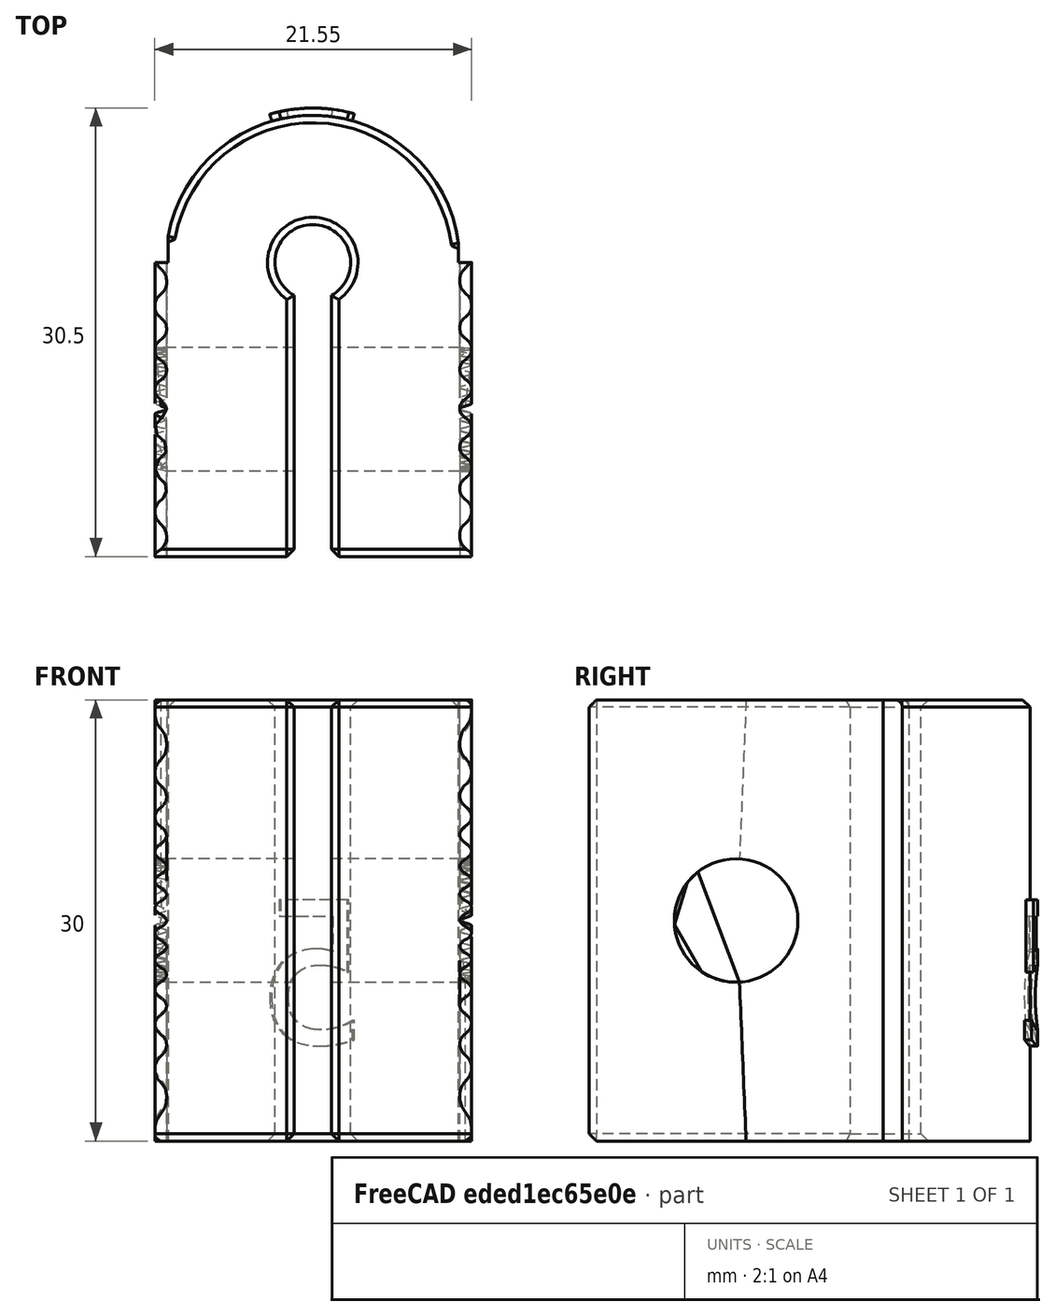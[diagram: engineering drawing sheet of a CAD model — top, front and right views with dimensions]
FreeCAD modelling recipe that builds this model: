
FCSTD DOCUMENT  (FreeCAD 1.1R42945 (Git))
Label: Pin clamp
License: All rights reserved
LicenseURL: https://en.wikipedia.org/wiki/All_rights_reserved
objects: Part::FeaturePython×3, App::Point×3, PartDesign::Body×3, Sketcher::SketchObject×2, PartDesign::FeatureBase×2, Mesh::Feature×1, Spreadsheet::Sheet×1, Part::RuledSurface×1, Part::Extrusion×1, Part::Box×1, Part::MultiCommon×1, Part::Part2DObjectPython×1, Part::Cylinder×1, PartDesign::Pad×1, Part::MultiFuse×1, Part::Chamfer×1, Part::Cut×1
note: 26 computed .brp shape members not serialized (recipe doc carries the construction recipe); baked Part::Feature solids carry a one-line shape summary decoded from their .brp

FEATURE [Mesh::Feature] PINCLAMP_5MM
  Placement = pos=(0,0,-30) rot=(0,0,-1;1.5708rad)
FEATURE [Spreadsheet::Sheet] Spreadsheet  label="Parameters"
  cells = A1='Description of parameter; B1='Measurement; A2='Bolt diameter (mm); B2(bolt)=8; A3='Bolt diameter tolerance (mm); B3(BoltTolerance)=0.4; A4='Pin diameter (mm); B4(pin)=5; A5='Pin diameter tolerance (mm); B5(PinTolerance)=0.15; A7='Interface parameters; A8='Inner radius; B8(InnerRadius)=2; A9='Outer radius; B9(OuterRadius)=20; A10='Amplitude of waves; B10(amplitude)=0.8; A11='Number of waves; B11(NumberOfWaves)=36; A12='Interval (do not change); B12(Interval)=0.01
FEATURE [Part::FeaturePython] ParametricCurve  # WARN: FeaturePython — macro-defined, semantics opaque (R4)
  AttacherType = Attacher::AttachEngine3D
  Closed = false
  Continuity = C2
  EditFormulas = false
  F_X = 0
  F_Y = 0
  F_Z = 0
  F_a = 20
  F_b = 36
  F_c = 0.8
  F_d = [0,0]
  FormulaName = formula1
  Formulas = 0
  Interval = 0.01
  MakeFace = false
  PlusOneIteration = true
  Points = (630) [(20,0,0.4),(19.999,0.199997,0.602621),(19.996,0.399973,0.738292),(19.991,0.59991,0.791969),(19.984,0.799787,0.799956),(19.975,0.999583,0.799593),+624 more]
  ShapeType = 0
  Sorted = false
  UpdateSpreadsheet = false
  UseSpreadsheet = false
  Version = 2023.05.06
  X = a*cos(t)
  Y = a*sin(t)
  Z = c * ( 3*((1 + sin(b*t))/2)^2 - 2*((1 + sin(b*t))/2)^3 )
  a = 20
  b = 36
  c = 0.8
  t_max = 6.28319
  t_min = 0
  expr: Interval = .Spreadsheet.Interval
FEATURE [Part::FeaturePython] ParametricCurve001  # WARN: FeaturePython — macro-defined, semantics opaque (R4)
  AttacherType = Attacher::AttachEngine3D
  Closed = false
  Continuity = C2
  EditFormulas = false
  F_X = 0
  F_Y = 0
  F_Z = 0
  F_a = 2
  F_b = 36
  F_c = 0.8
  F_d = [0,0]
  FormulaName = formula2
  Formulas = 0
  Interval = 0.01
  MakeFace = false
  PlusOneIteration = true
  Points = (630) [(2,0,0.4),(1.9999,0.0199997,0.602621),(1.9996,0.0399973,0.738292),(1.9991,0.059991,0.791969),(1.9984,0.0799787,0.799956),(1.9975,0.0999583,0.799593),+624 more]
  ShapeType = 0
  Sorted = false
  UpdateSpreadsheet = false
  UseSpreadsheet = false
  Version = 2023.05.06
  X = a*cos(t)
  Y = a*sin(t)
  Z = c * ( 3*((1 + sin(b*t))/2)^2 - 2*((1 + sin(b*t))/2)^3 )
  a = 2
  b = 36
  c = 0.8
  t_max = 6.28319
  t_min = 0
  expr: Interval = .Spreadsheet.Interval
  expr: a = .Spreadsheet.InnerRadius
  expr: b = .Spreadsheet.NumberOfWaves
  expr: c = .Spreadsheet.amplitude
FEATURE [Part::RuledSurface] Ruled_Surface
  Curve1 = -> ParametricCurve [Edge1]
  Curve2 = -> ParametricCurve001 [Edge1]
  Orientation = 0
  Placement = pos=(10,-4.94766,-14.9986) rot=(0.020938,0.999562,0.020938;1.57123rad)
FEATURE [Part::Extrusion] Extrude003
  Base = -> Ruled_Surface
  Dir = (-1,0,0)
  DirMode = 0
  FaceMakerClass = Part::FaceMakerBullseye
  FaceMakerMode = 3
  LengthFwd = 2
  LengthRev = 0
  Solid = false
  Symmetric = false
FEATURE [Part::Box] Box  label="Cube"
  AttacherType = Attacher::AttachEngine3D
  Height = 1.5
  Length = 30
  Placement = pos=(9.4513,-15,0) rot=(0,1,0;1.5708rad)
  Width = 20
FEATURE [Part::MultiCommon] Common
  Placement = pos=(0,0,-30) rot=(0,1,0;3.14159rad)
  Shapes = -> [Box,Extrude003]
FEATURE [Part::Part2DObjectPython] ShapeString  # Draft 2D object (typed FeaturePython)
  FontFile = <path>
  Fuse = false
  Justification = 4
  JustificationReference = 0
  KeepLeftMargin = false
  MakeFace = true
  ObliqueAngle = 0
  Placement = pos=(30,4.85425,0) rot=(0,0,1;0rad)
  ScaleToSize = true
  Size = 16
  String = 5
  Tracking = 0
FEATURE [Part::Cylinder] Cylinder
  Angle = 360
  AttacherType = Attacher::AttachEngine3D
  FirstAngle = 0
  Height = 30
  Placement = pos=(-15,-5,-15) rot=(0,1,0;1.5708rad)
  Radius = 4.2
  SecondAngle = 0
  expr: Radius = (Spreadsheet.bolt + Spreadsheet.BoltTolerance) / 2
FEATURE [Sketcher::SketchObject] Sketch
  ArcFitTolerance = 1e-06
  AttachmentSupport = -> [Origin]
  ExternalTypes = [0]
  FullyConstrained = false
  MakeInternals = false
  MapMode = 5
  expr: Constraints[16] = (Spreadsheet.pin + Spreadsheet.PinTolerance) / 2
  sketch-geometry (8):
    g0: LineSegment StartX=-9.84423 StartY=-15 StartZ=0 EndX=-9.84423 EndY=6.75819 EndZ=0
    g1: LineSegment StartX=-9.84423 StartY=-15 StartZ=0 EndX=-1.26513 EndY=-15 EndZ=0
    g2: LineSegment StartX=-1.26513 StartY=-15 StartZ=0 EndX=-1.26513 EndY=2.75722 EndZ=0
    g3: LineSegment StartX=1.26513 StartY=2.75722 StartZ=0 EndX=1.26513 EndY=-15 EndZ=0
    g4: LineSegment StartX=1.26513 StartY=-15 StartZ=0 EndX=9.91461 EndY=-15 EndZ=0
    g5: LineSegment StartX=9.91461 StartY=-15 StartZ=0 EndX=9.91461 EndY=6.30402 EndZ=0
    g6: ArcOfCircle CenterX=0 CenterY=5 CenterZ=0 NormalX=0 NormalY=0 NormalZ=1 AngleXU=0 Radius=10 StartAngle=0.130774 EndAngle=2.96485
    g7: ArcOfCircle CenterX=0 CenterY=5 CenterZ=0 NormalX=0 NormalY=0 NormalZ=1 AngleXU=0 Radius=2.575 StartAngle=5.22598 EndAngle=10.482
  constraints (22):
    c: Vertical(g0)
    c: Coincident(g0,g1)
    c: Horizontal(g1)
    c: Coincident(g1,g2)
    c: Vertical(g3)
    c: Coincident(g3,g4)
    c: Horizontal(g4)
    c: Coincident(g4,g5)
    c: Vertical(g5)
    c: Coincident(g0,g6)
    c: Coincident(g6,g5)
    c: DistanceY(g3,g-1) = 15
    c: DistanceY(g1,g-1) = 15
    c: Coincident(g3,g7)
    c: Vertical(g2)
    c: Coincident(g7,g2)
    c: Radius(g7) = 2.575
    c: PointOnObject(g7,g-2)
    c: Coincident(g6,g7)
    c: DistanceY(g2,g3) = 0
    c: DistanceY(g3,g6) = 20
    c: Radius(g6) = 10
FEATURE [PartDesign::Pad] Pad
  Direction = (0,0,1)
  Length = 30
  Length2 = 10
  Profile = -> Sketch
  ReferenceAxis = -> Sketch [N_Axis]
  Refine = true
  Reversed = true
  Suppressed = false
  Type = 0
FEATURE [Sketcher::SketchObject] Mapped_Sketch
  ArcFitTolerance = 1e-06
  AttachmentSupport = -> [Pad]
  ExternalTypes = [0]
  FullyConstrained = false
  MakeInternals = false
  Placement = pos=(3.03142,5.20342,0) rot=(0,0,1;0rad)
  sketch-geometry (8):
    g0: LineSegment [constr] StartX=0 StartY=0 StartZ=0 EndX=27.0812 EndY=0 EndZ=0
    g1: LineSegment [constr] StartX=27.0812 StartY=0 StartZ=0 EndX=27.0812 EndY=30 EndZ=0
    g2: LineSegment [constr] StartX=27.0812 StartY=30 StartZ=0 EndX=0 EndY=30 EndZ=0
    g3: LineSegment [constr] StartX=0 StartY=30 StartZ=0 EndX=0 EndY=0 EndZ=0
    g4: LineSegment [constr] StartX=10.2789 StartY=6.24604 StartZ=0 EndX=10.2789 EndY=-19.2688 EndZ=0
    g5: LineSegment [constr] StartX=10.2789 StartY=-19.2688 StartZ=0 EndX=52.8869 EndY=-19.2688 EndZ=0
    g6: LineSegment [constr] StartX=52.8869 StartY=-19.2688 StartZ=0 EndX=52.8869 EndY=6.24604 EndZ=0
    g7: LineSegment [constr] StartX=52.8869 StartY=6.24604 StartZ=0 EndX=10.2789 EndY=6.24604 EndZ=0
  constraints (19):
    c: Coincident(g0,g-1)
    c: Coincident(g0,g1)
    c: Coincident(g1,g2)
    c: Coincident(g2,g3)
    c: Coincident(g3,g0)
    c: Horizontal(g0)
    c: Horizontal(g2)
    c: Vertical(g1)
    c: Vertical(g3)
    c: DistanceX(g2,g2) = 27.0812
    c: DistanceY(g1,g1) = 30
    c: Coincident(g4,g5)
    c: Coincident(g5,g6)
    c: Coincident(g6,g7)
    c: Coincident(g7,g4)
    c: Vertical(g4)
    c: Vertical(g6)
    c: Horizontal(g5)
    c: Horizontal(g7)
FEATURE [App::Point] Origin001
  Role = Origin
FEATURE [PartDesign::Body] Body  label="Main clamp body"
  AllowCompound = false
  Group = -> [Sketch,Pad]
  Origin = -> Origin
  Tip = -> Pad
FEATURE [Part::FeaturePython] Sketch_On_Surface  # WARN: FeaturePython — macro-defined, semantics opaque (R4)
  ConstructionBounds = true
  ExtraObjects = -> [ShapeString]
  FillExtrusion = true
  FillFaces = true
  ReverseU = false
  ReverseV = false
  Sketch = -> Mapped_Sketch
  SwapUV = false
  Thickness = 0.5
FEATURE [PartDesign::FeatureBase] Clone
  BaseFeature = -> Common
  Suppressed = false
FEATURE [App::Point] Origin003
  Role = Origin
FEATURE [PartDesign::Body] Body001  label="Interface 1"
  AllowCompound = false
  Group = -> [Clone]
  Origin = -> Origin002
  Tip = -> Clone
FEATURE [PartDesign::FeatureBase] Clone001
  BaseFeature = -> Common
  Placement = pos=(0.0566779,0,-30) rot=(0,0,0;3.14159rad)
  Suppressed = false
FEATURE [App::Point] Origin005
  Role = Origin
FEATURE [PartDesign::Body] Body002  label="Interface 2"
  AllowCompound = false
  Group = -> [Clone001]
  Origin = -> Origin004
  Tip = -> Clone001
FEATURE [Part::MultiFuse] Fusion
  Shapes = -> [Body,Sketch_On_Surface,Body001,Body002]
FEATURE [Part::Chamfer] Chamfer
  Base = -> Fusion
  EdgeLinks = -> Fusion [Edge3,Edge4,Edge5,Edge6,Edge7,Edge8,Edge9,Edge10,Edge11,?Edge15,Edge19,Edge20,Edge21,Edge28]
  Edges = 14 edges r=0.5: [Edge3,Edge4,Edge5,Edge6,Edge7,Edge8,Edge9,Edge10,Edge11,Edge15,Edge19,Edge20,Edge21,Edge28]
FEATURE [Part::Cut] Cut
  Base = -> Chamfer
  Tool = -> Cylinder
note: 1 file-system path scrubbed to <path> (originals preserved in the JSON sidecar)
